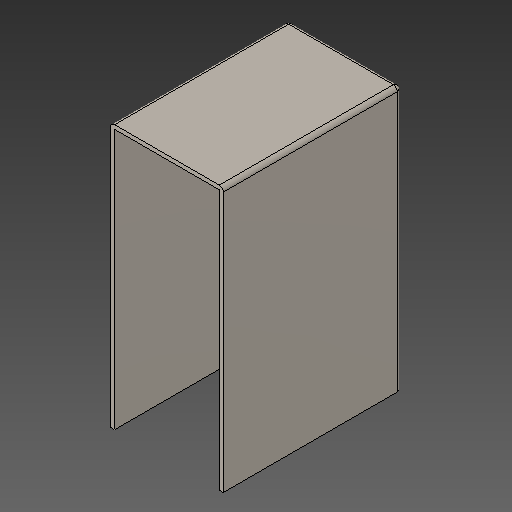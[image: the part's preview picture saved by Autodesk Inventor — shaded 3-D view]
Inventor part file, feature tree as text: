
AUTODESK INVENTOR PART (.ipt)
format: ipt  version: 2018.2 (Build 222227000, 227)  size: 90,112 bytes
history: native  units: mm
features: other x1, shell x1
ambient origin geometry x8: Origin, YZ Plane, XZ Plane, XY Plane, X Axis, Y Axis, Z Axis, Center Point
bodies: Body1 (feature_tree)
feature tree (2):
  other  "ソリッド1"
  shell  "Shell1"  [1 undecoded]
note: 1 required parameter value undecoded (feature->parameter linkage not recoverable at this tier; creation-order binding heuristic only, values carry confidence <= 0.55)
